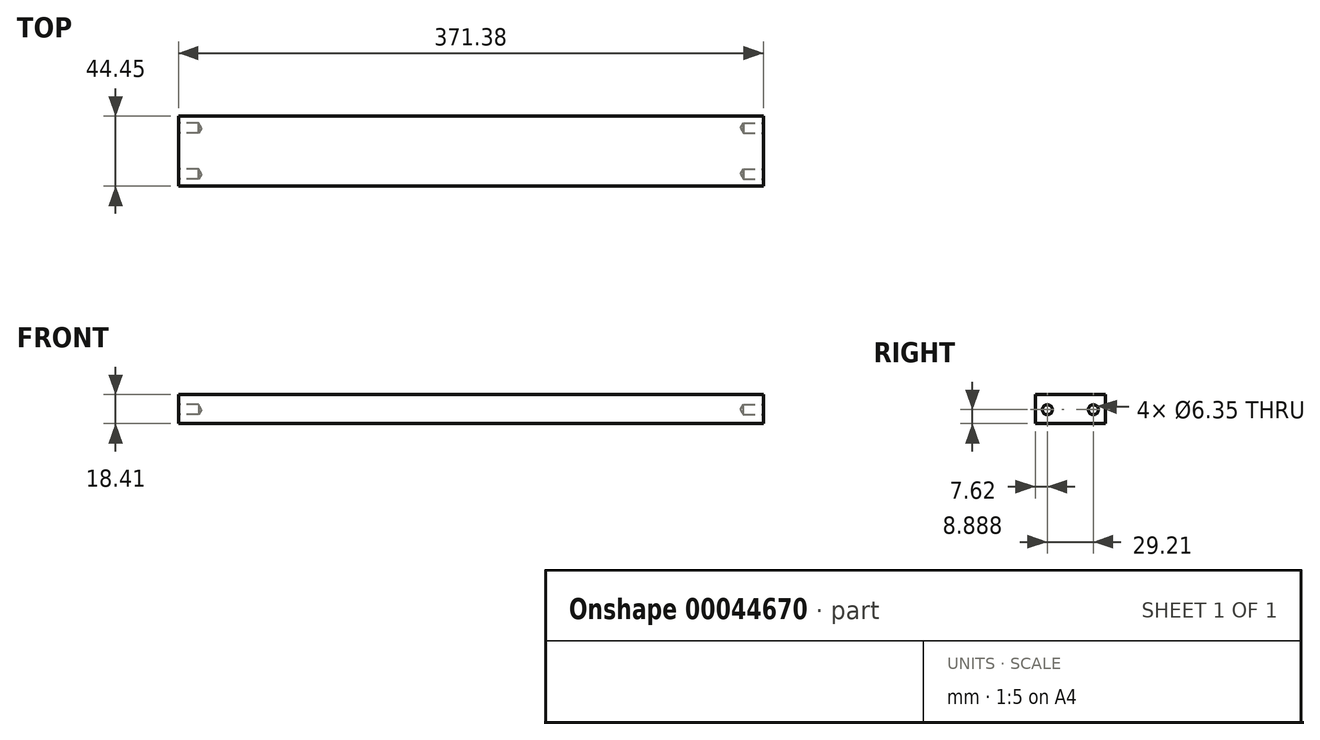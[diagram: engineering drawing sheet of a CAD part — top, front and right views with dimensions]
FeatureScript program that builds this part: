
annotation { "Feature Type Name" : "Feature", "Feature Type Description" : "" }
export const myFeature = defineFeature(function(context is Context, id is Id, definition is map)
    precondition{}
    {
        {
            var Q0;
            Q0=qCreatedBy(makeId("Front.planeOp"),FACE);
            var sketch = newSketch(context, id + "F0", { "sketchPlane" : qUnion([Q0])});
            skLineSegment(sketch, "E0.bottom", {"start": v(-111.96, -0.69) * mm, "end": v(259.42, -0.69) * mm});
            skLineSegment(sketch, "E0.top", {"start": v(-111.96, -19.1) * mm, "end": v(259.42, -19.1) * mm});
            skLineSegment(sketch, "E0.left", {"start": v(-111.96, -0.69) * mm, "end": v(-111.96, -19.1) * mm});
            skLineSegment(sketch, "E0.right", {"start": v(259.42, -0.69) * mm, "end": v(259.42, -19.1) * mm});
            skSolve(sketch);
        }
        {
            var Q0;
            Q0 = qSketchRegion(id + "F0", true);
            extrude(context, id + "F1", {"entities" : qUnion([Q0]), "depth" : 44.45 * mm});
        }
        {
            var Q0;
            Q0=makeQuery(id+"F1.opExtrude","SWEPT_FACE",FACE,{"disambiguationData":[OSD([sQuery(id+"F0.wireOp",EDGE,"E0.right")])]});
            var sketch = newSketch(context, id + "F2", { "sketchPlane" : qUnion([Q0])});
            skPoint(sketch, "E1", {"position": v(-7.62, -10.21) * mm});
            skSolve(sketch);
        }
        {
            var Q0;
            {var subQ0=sQuery(id+"F0.wireOp",EDGE,"E0.right");Q0=makeQuery(id+"F2.imprint","IMPRINT",FACE,{"disambiguationData":[TD([[makeQuery(id+"F2.imprint","IMPRINT",EDGE,{"derivedFrom":makeQuery(id+"F1.opExtrude","CAP_EDGE",EDGE,{"disambiguationData":[OSD([subQ0])],"isStart":true})}),-1.0]])]});}
            var sketch = newSketch(context, id + "F3", { "sketchPlane" : qUnion([Q0])});
            skPoint(sketch, "E2", {"position": v(-36.83, -10.21) * mm});
            skSolve(sketch);
        }
        {
            var Q0;
            Q0=makeQuery(id+"F1.opExtrude","SWEPT_FACE",FACE,{"disambiguationData":[OSD([sQuery(id+"F0.wireOp",EDGE,"E0.left")])]});
            var sketch = newSketch(context, id + "F4", { "sketchPlane" : qUnion([Q0])});
            skPoint(sketch, "E3", {"position": v(7.62, -10.21) * mm});
            skPoint(sketch, "E4", {"position": v(36.83, -10.21) * mm});
            skSolve(sketch);
        }
        {
            var Q0;
            Q0=sQuery(id+"F4.wireOp",VERTEX,"E3");
            var Q1;
            Q1=sQuery(id+"F4.wireOp",VERTEX,"E4");
            var Q2;
            Q2=sQuery(id+"F3.wireOp",VERTEX,"E2");
            var Q3;
            Q3=sQuery(id+"F2.wireOp",VERTEX,"E1");
            var Q4;
            Q4=makeQuery(id+"F1.opExtrude","SWEPT_BODY",BODY,{"disambiguationData":[OSD([sQuery(id+"F0.wireOp",EDGE,"E0.bottom"),sQuery(id+"F0.wireOp",EDGE,"E0.top"),sQuery(id+"F0.wireOp",EDGE,"E0.left"),sQuery(id+"F0.wireOp",EDGE,"E0.right")])]});
            hole(context, id + "F5", {"style" : HoleStyle.SIMPLE, "holeDiameter" : 6.35 * mm, "endStyle" : HoleEndStyle.BLIND, "holeDepth" : 12.7 * mm, "locations" : qUnion([Q0, Q1, Q2, Q3]), "scope" : qUnion([Q4])});
        }
    });
